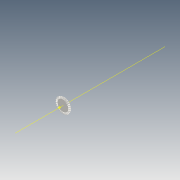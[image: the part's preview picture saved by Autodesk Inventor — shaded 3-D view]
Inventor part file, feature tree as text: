
AUTODESK INVENTOR PART (.ipt)
format: ipt  version: 2021 (Build 250183000, 183)  size: 532,992 bytes
history: native  units: mm
features: other x16, sketch x10, loft x3, pattern_circular x3, extrude x1
ambient origin geometry x6: Origin, XZ Plane, X Axis, Y Axis, Z Axis, Center Point
bodies: Solid1 (feature_tree)
feature tree (33):
  other  "Ponto superior"
  other  "Plano de malha 2"
  other  "Corpo dentado"
  other  "Ponto inicial"
  other  "Plano de dente"
  sketch  "Esboço inicial"  dims[d3=0.6mm]
  other  "Extremidade"
  loft  "Loft"
  pattern_circular  "Circular Pattern"  [2 undecoded]
  sketch  "Esboço 3D direito"  dims[d4=1.194087mm]
  other  "Plano final direito"
  loft  "Transição direita"
  pattern_circular  "Padrão circular direito"  Angle=90.0deg  [1 undecoded]
  sketch  "Esboço 3D esquerdo"  dims[d5=90.0deg]
  other  "Plano final esquerdo"
  loft  "Transição esquerda"
  pattern_circular  "Padrão circular esquerdo"  Angle=360.0deg  [1 undecoded]
  other  "Fixar corpo"
  extrude  "Extrusão1"  Depth=10.0mm
  other  "Plano de malha"
  other  "Plano superior"
  sketch  "Esboço de corpo dentado"  dims[d7=1.663639mm]
  other  "Plano final"
  sketch  "Esboço final"  dims[d8=1.691227mm]
  other  "Helical Curve Left"
  sketch  "Esboço final esquerdo"  dims[d9=4.071779mm]
  sketch  "Esboço de corpo"  dims[d11=0.6198mm]
  sketch  "Sketch6"  dims[d0=4.68mm d1=4.46412mm]
  other  "Srf1"
  other  "Helical Curve Right"
  sketch  "Esboço final direita"  dims[d12=1.281954mm d15=1.303212mm d16=3.137599mm d17=0.0mm d18=90.0deg d19=0.0mm d20=90.0deg d21=260.0mm d22=360.0deg d26=17.944705mm d27=0.309728mm d28=4.68mm d29=-10.47518mm d30=1.281954mm d31=1.303212mm d32=3.137599mm d35=0.0mm d37=0.0mm d39=0.0mm d40=90.0deg d41=260.0mm d42=360.0deg d46=90.0deg d47=90.0deg d48=0.0mm d49=0.0mm d50=90.0deg d51=1.208305mm d52=0.0mm d53=0.0mm d54=0.0mm d56=0.94732mm d57=4.981399mm d58=4.419079mm d59=3.838526mm d60=3.405218mm d61=3.838526mm d62=3.405218mm d65=17.944705mm d66=31.5mm d67=4.68mm d68=-10.47518mm d69=0.309728mm d70=1.303212mm d71=3.137599mm d72=1.281954mm d73=3.405218mm d74=3.838526mm d75=0.0mm d77=0.0mm d79=0.0mm d80=90.0deg d81=260.0mm d82=360.0deg d84=10.0mm d85=20.0mm d86=20.0mm d87=10.0mm d88=0.0mm d89=0.0mm d90=90.0deg d91=90.0deg d92=90.0deg d93=90.0deg d94=11.5mm d95=0.0mm]
  sketch  "Esboço8"  dims[d2=4.8599mm]
  other  "Diâmetro do flanco"
note: 4 required parameter values undecoded (feature->parameter linkage not recoverable at this tier; creation-order binding heuristic only, values carry confidence <= 0.55)
